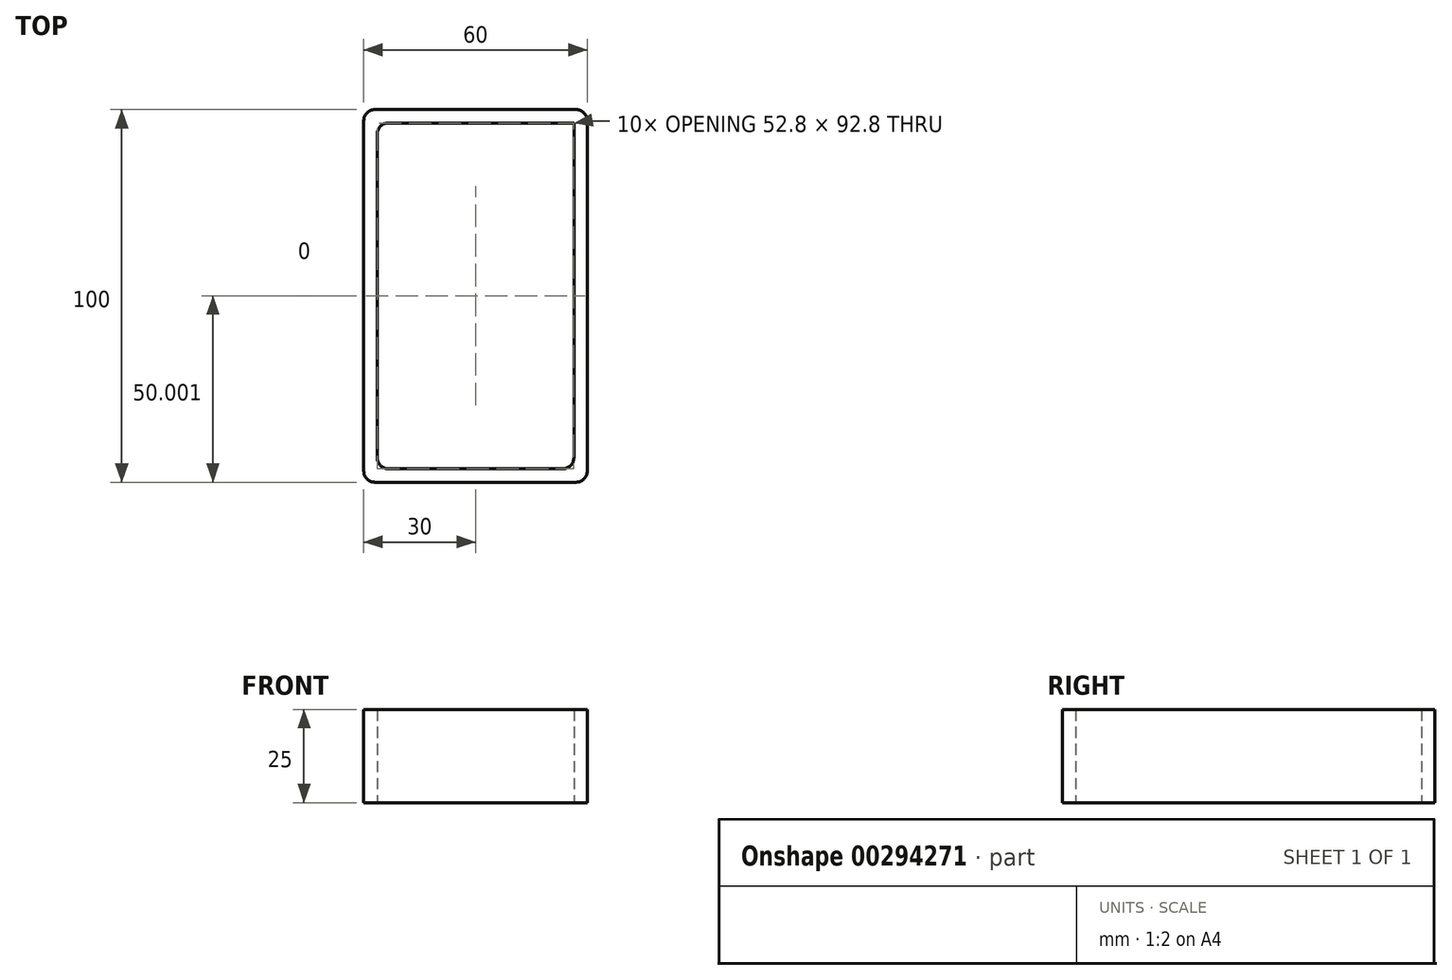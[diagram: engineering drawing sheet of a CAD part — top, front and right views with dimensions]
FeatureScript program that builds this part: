
annotation { "Feature Type Name" : "Feature", "Feature Type Description" : "" }
export const myFeature = defineFeature(function(context is Context, id is Id, definition is map)
    precondition{}
    {
        {
            var Q0;
            Q0=qCreatedBy(makeId("Top.planeOp"),FACE);
            var sketch = newSketch(context, id + "F0", { "sketchPlane" : qUnion([Q0])});
            skLineSegment(sketch, "E0", {"start": v(56.4, 120.05) * mm, "end": v(56.4, 26.05) * mm});
            skLineSegment(sketch, "E1", {"start": v(53.4, 23.05) * mm, "end": v(-0.6, 23.05) * mm});
            skLineSegment(sketch, "E2", {"start": v(-3.6, 23.05) * mm, "end": v(-3.6, 120.05) * mm});
            skLineSegment(sketch, "E3", {"start": v(-0.6, 123.05) * mm, "end": v(53.4, 123.05) * mm});
            skLineSegment(sketch, "E4", {"start": v(-3.6, 26.05) * mm, "end": v(-3.6, 73.05) * mm});
            skLineSegment(sketch, "E5", {"start": v(0, 73.05) * mm, "end": v(0, 119.45) * mm});
            skLineSegment(sketch, "E6", {"start": v(0, 116.45) * mm, "end": v(0, 29.65) * mm});
            skPoint(sketch, "E7.endSnap0", {"position": v(56.4, 73.05) * mm});
            skLineSegment(sketch, "E8", {"start": v(52.8, 73.05) * mm, "end": v(52.8, 119.45) * mm});
            skLineSegment(sketch, "E9", {"start": v(52.8, 119.45) * mm, "end": v(52.8, 29.65) * mm});
            skLineSegment(sketch, "E10", {"start": v(49.8, 26.65) * mm, "end": v(3, 26.65) * mm});
            skLineSegment(sketch, "E11", {"start": v(52.8, 119.45) * mm, "end": v(3, 119.45) * mm});
            skPoint(sketch, "E12.visualSharp", {"position": v(56.4, 123.05) * mm});
            skArc(sketch, "E12.filletArc", {"start": v(56.4, 120.05) * mm, "mid": v(55.52, 122.17) * mm, "end": v(53.4, 123.05) * mm});
            skPoint(sketch, "E13.visualSharp", {"position": v(0, 119.45) * mm});
            skArc(sketch, "E13.filletArc", {"start": v(3, 119.45) * mm, "mid": v(0.88, 118.57) * mm, "end": v(0, 116.45) * mm});
            skPoint(sketch, "E14.visualSharp", {"position": v(0, 26.65) * mm});
            skArc(sketch, "E14.filletArc", {"start": v(0, 29.65) * mm, "mid": v(0.88, 27.53) * mm, "end": v(3, 26.65) * mm});
            skPoint(sketch, "E15.visualSharp", {"position": v(52.8, 26.65) * mm});
            skArc(sketch, "E15.filletArc", {"start": v(49.8, 26.65) * mm, "mid": v(51.92, 27.53) * mm, "end": v(52.8, 29.65) * mm});
            skPoint(sketch, "E16.visualSharp", {"position": v(56.4, 23.05) * mm});
            skArc(sketch, "E16.filletArc", {"start": v(53.4, 23.05) * mm, "mid": v(55.52, 23.93) * mm, "end": v(56.4, 26.05) * mm});
            skPoint(sketch, "E17.visualSharp", {"position": v(-3.6, 23.05) * mm});
            skArc(sketch, "E17.filletArc", {"start": v(-3.6, 26.05) * mm, "mid": v(-2.72, 23.93) * mm, "end": v(-0.6, 23.05) * mm});
            skPoint(sketch, "E18.visualSharp", {"position": v(-3.6, 123.05) * mm});
            skArc(sketch, "E18.filletArc", {"start": v(-0.6, 123.05) * mm, "mid": v(-2.72, 122.17) * mm, "end": v(-3.6, 120.05) * mm});
            skPoint(sketch, "E7.start.orphan", {"position": v(56.4, 73.05) * mm});
            skSolve(sketch);
        }
        {
            var Q0;
            Q0 = qSketchRegion(id + "F0", true);
            extrude(context, id + "F1", {"entities" : qUnion([Q0]), "depth" : 25 * mm});
        }
    });
